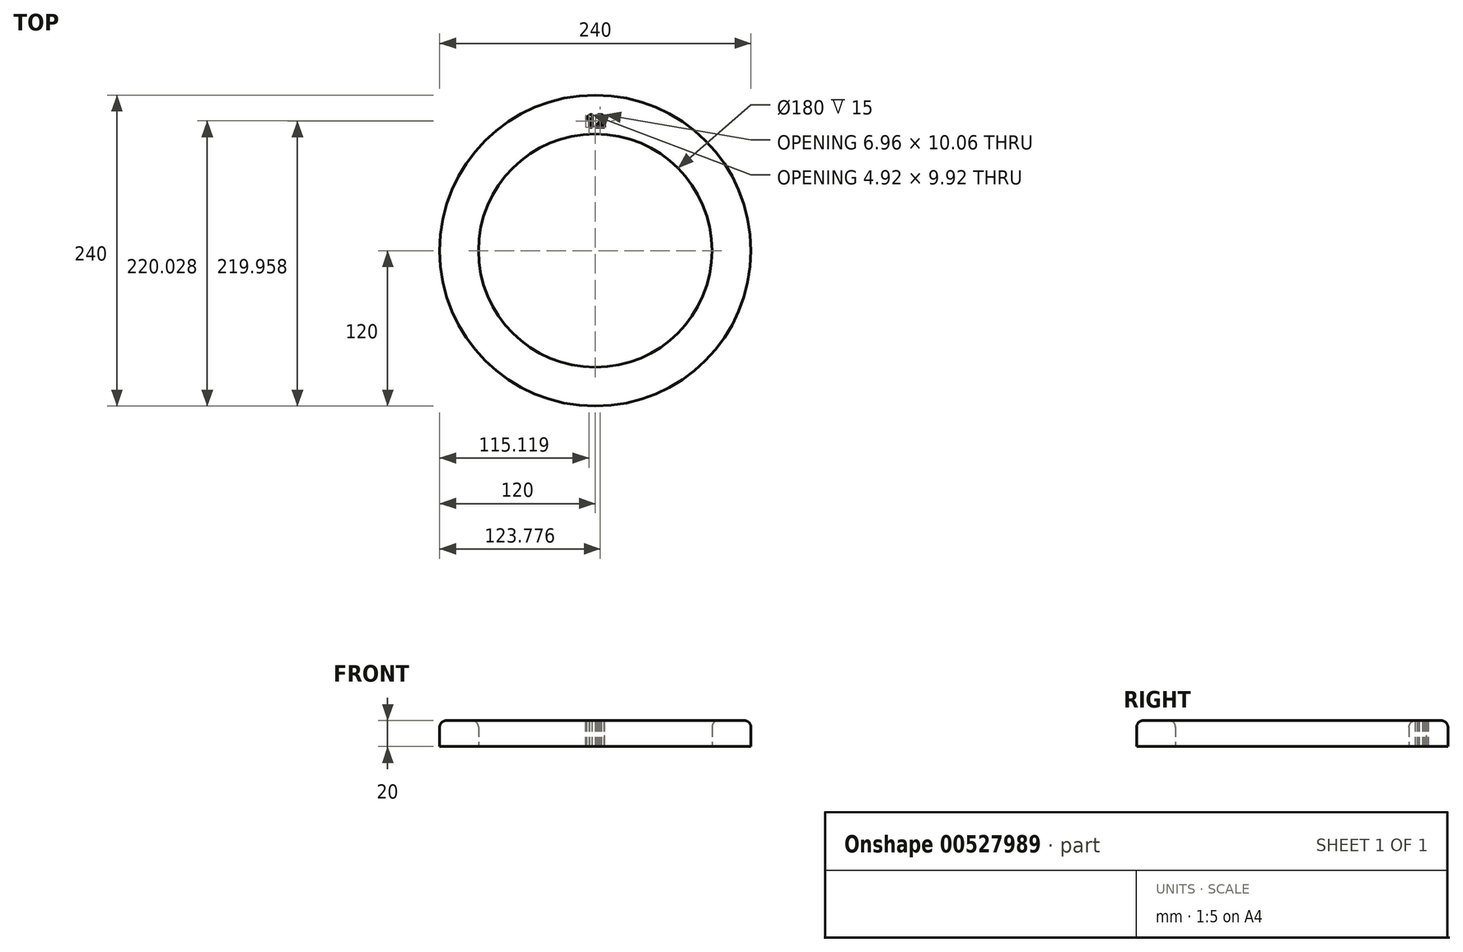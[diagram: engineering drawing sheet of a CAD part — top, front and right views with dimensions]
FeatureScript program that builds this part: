
annotation { "Feature Type Name" : "Feature", "Feature Type Description" : "" }
export const myFeature = defineFeature(function(context is Context, id is Id, definition is map)
    precondition{}
    {
        {
            var Q0;
            Q0=qCreatedBy(makeId("Top.planeOp"),FACE);
            var sketch = newSketch(context, id + "F0", { "sketchPlane" : qUnion([Q0])});
            skCircle(sketch, "E0", {"center": v(0, 0) * mm, "radius": 120 * mm});
            skCircle(sketch, "E1", {"center": v(0, 0) * mm, "radius": 90 * mm});
            skSolve(sketch);
        }
        {
            var Q0;
            Q0=qSketchRegion(id+"F0",true);
            extrude(context, id + "F1", {"entities" : qUnion([Q0]), "depth" : 20 * mm});
        }
        {
            var Q0;
            Q0=makeQuery(id+"F1.opExtrude","CAP_FACE",FACE,{"disambiguationData":[OSD([sQuery(id+"F0.wireOp",EDGE,"E0"),sQuery(id+"F0.wireOp",EDGE,"E1")])],"isStart":false});
            var sketch = newSketch(context, id + "F2", { "sketchPlane" : qUnion([Q0])});
            skText(sketch, "E2", { "text": "12", "fontName": "OpenSans-Bold.ttf"});
            skLineSegment(sketch, "E3", {"start": v(0, 92.68) * mm, "end": v(0, -90.1) * mm, "construction": true});
            skLineSegment(sketch, "E4", {"start": v(93.53, 0) * mm, "end": v(-89.46, 0) * mm, "construction": true});
            const initialGuessF2  = {"E2": [-0.00816, 0.095, 1, 0, 0.01]};
            skSetInitialGuess(sketch, initialGuessF2);
            skSolve(sketch);
        }
        {
            var Q0;
            Q0=qSketchRegion(id+"F2",true);
            extrude(context, id + "F3", {"entities" : qUnion([Q0]), "operationType" : NewBodyOperationType.REMOVE, "oppositeDirection" : true, "depth" : 25 * mm});
        }
        {
            var Q0;
            Q0=makeQuery(id+"F1.opExtrude","CAP_EDGE",EDGE,{"disambiguationData":[OSD([sQuery(id+"F0.wireOp",EDGE,"E1")])],"isStart":false});
            var Q1;
            Q1=makeQuery(id+"F1.opExtrude","CAP_EDGE",EDGE,{"disambiguationData":[OSD([sQuery(id+"F0.wireOp",EDGE,"E0")])],"isStart":false});
            fillet(context, id + "F4", {"entities" : qUnion([Q0, Q1]), "radius" : 5 * mm, "tangentPropagation" : true, "allowEdgeOverflow" : false});
        }
    });
